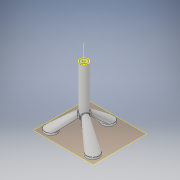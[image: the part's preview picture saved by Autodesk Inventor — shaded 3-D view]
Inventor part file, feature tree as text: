
AUTODESK INVENTOR PART (.ipt)
format: ipt  version: 2018 (Build 220112000, 112)  size: 536,064 bytes
history: native  units: in
note: dims shown in document units (in); Inventor stores cm internally (conversion verified against a paired STEP export)
features: plane x4, sketch x4, extrude x3, other x3, fillet x2, loft x1, pattern_circular x1, projected_geometry x1
ambient origin geometry x8: Origin, YZ Plane, XZ Plane, XY Plane, X Axis, Y Axis, Z Axis, Center Point
bodies: Solid1 (feature_tree)
feature tree (19):
  plane  "Work Plane1"
  extrude  "Extrusion1"  Depth=4.3307in
  plane  "Work Plane2"
  extrude  "Extrusion2"  Depth=0.75in
  plane  "Work Plane6"
  sketch  "Sketch4"  dims[d4=0.125in d5=0.0in d6=1.0in]
  other  "Work Axis1"
  extrude  "Extrusion5"  Depth=1.0in
  loft  "Loft3"
  fillet  "Fillet1"  Radius=3.0in
  pattern_circular  "Circular Pattern2"  [2 undecoded]
  fillet  "Fillet2"  Radius=0.38in
  sketch  "Sketch5"  dims[d7=0.25in d8=0.125in d9=3.0in d10=0.0in d14=-0.0375in d16=0.38in d32=0.0938in d33=0.0in d34=0.0in d35=90.0deg d36=0.0in d37=90.0deg d38=1.1811in d39=360.0deg d41=0.0312in d42=0.0312in]
  sketch  "Sketch1"  dims[d0=4.7244in d1=4.3307in]
  sketch  "Sketch2"  dims[d2=1.5in d3=0.75in]
  plane  "Work Plane5"
  other  "Edges5"
  other  "Edges6"
  projected_geometry  "Project Cut Edges3"
note: 2 required parameter values undecoded (feature->parameter linkage not recoverable at this tier; creation-order binding heuristic only, values carry confidence <= 0.55)
